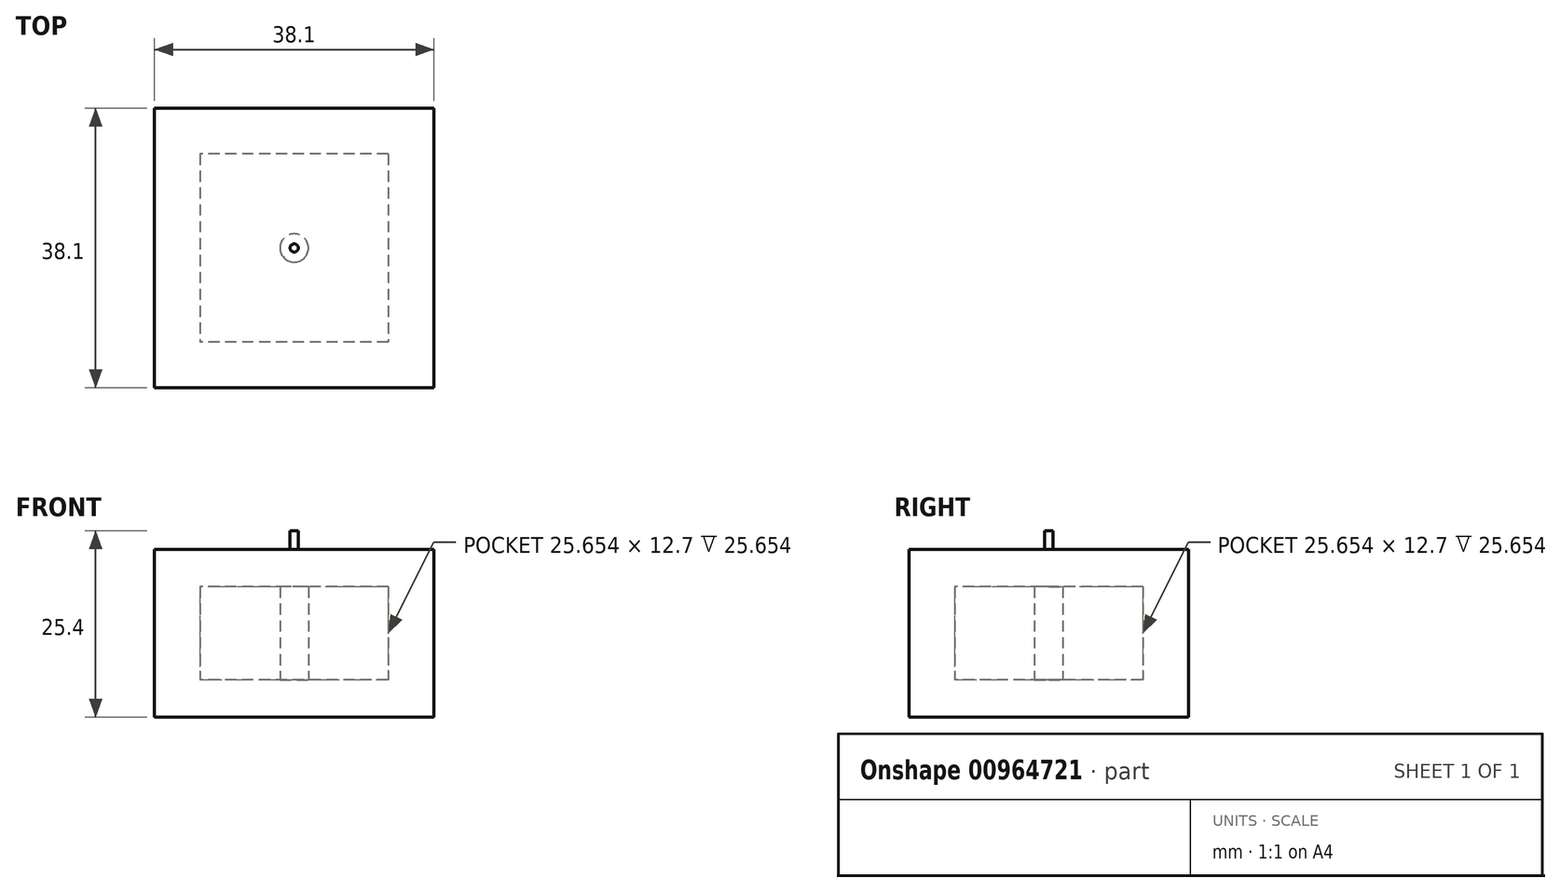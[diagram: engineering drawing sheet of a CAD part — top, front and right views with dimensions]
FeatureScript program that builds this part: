
annotation { "Feature Type Name" : "Feature", "Feature Type Description" : "" }
export const myFeature = defineFeature(function(context is Context, id is Id, definition is map)
    precondition{}
    {
        {
            var Q0;
            Q0=qCreatedBy(makeId("Top.planeOp"),FACE);
            var sketch = newSketch(context, id + "F0", { "sketchPlane" : qUnion([Q0])});
            skLineSegment(sketch, "E0.bottom", {"start": v(19.05, 19.05) * mm, "end": v(-19.05, 19.05) * mm});
            skLineSegment(sketch, "E0.top", {"start": v(19.05, -19.05) * mm, "end": v(-19.05, -19.05) * mm});
            skLineSegment(sketch, "E0.left", {"start": v(19.05, 19.05) * mm, "end": v(19.05, -19.05) * mm});
            skLineSegment(sketch, "E0.right", {"start": v(-19.05, 19.05) * mm, "end": v(-19.05, -19.05) * mm});
            skPoint(sketch, "E0.middle", {"position": v(0, 0) * mm});
            skSolve(sketch);
        }
        {
            var Q0;
            Q0=makeQuery(id+"F0.imprint","IMPRINT",FACE,{"disambiguationData":[TD([[makeQuery(id+"F0.imprint","IMPRINT",EDGE,{"derivedFrom":sQuery(id+"F0.wireOp",EDGE,"E0.bottom")}),1.0]])]});
            extrude(context, id + "F1", {"entities" : qUnion([Q0]), "depth" : 12.7 * mm, "offsetDistance" : 25.4 * mm});
        }
        {
            var Q0;
            Q0=qCreatedBy(makeId("Top.planeOp"),FACE);
            var sketch = newSketch(context, id + "F2", { "sketchPlane" : qUnion([Q0])});
            skLineSegment(sketch, "E1.bottom", {"start": v(12.83, 12.83) * mm, "end": v(-12.83, 12.83) * mm});
            skLineSegment(sketch, "E1.top", {"start": v(12.83, -12.83) * mm, "end": v(-12.83, -12.83) * mm});
            skLineSegment(sketch, "E1.left", {"start": v(12.83, 12.83) * mm, "end": v(12.83, -12.83) * mm});
            skLineSegment(sketch, "E1.right", {"start": v(-12.83, 12.83) * mm, "end": v(-12.83, -12.83) * mm});
            skPoint(sketch, "E1.middle", {"position": v(0, 0) * mm});
            skSolve(sketch);
        }
        {
            var Q0;
            Q0 = qSketchRegion(id + "F2", true);
            extrude(context, id + "F3", {"entities" : qUnion([Q0]), "operationType" : NewBodyOperationType.REMOVE, "depth" : 12.7 * mm, "offsetDistance" : 25.4 * mm});
        }
        {
            var Q0;
            Q0=makeQuery(id+"F1.opExtrude","CAP_FACE",FACE,{"disambiguationData":[OSD([sQuery(id+"F0.wireOp",EDGE,"E0.bottom"),sQuery(id+"F0.wireOp",EDGE,"E0.top"),sQuery(id+"F0.wireOp",EDGE,"E0.left"),sQuery(id+"F0.wireOp",EDGE,"E0.right")])],"isStart":false});
            var sketch = newSketch(context, id + "F4", { "sketchPlane" : qUnion([Q0])});
            skLineSegment(sketch, "E2.bottom", {"start": v(-19.05, -19.05) * mm, "end": v(19.05, -19.05) * mm});
            skLineSegment(sketch, "E2.top", {"start": v(-19.05, 19.05) * mm, "end": v(19.05, 19.05) * mm});
            skLineSegment(sketch, "E2.left", {"start": v(-19.05, -19.05) * mm, "end": v(-19.05, 19.05) * mm});
            skLineSegment(sketch, "E2.right", {"start": v(19.05, -19.05) * mm, "end": v(19.05, 19.05) * mm});
            skSolve(sketch);
        }
        {
            var Q0;
            Q0 = qSketchRegion(id + "F4", true);
            extrude(context, id + "F5", {"entities" : qUnion([Q0]), "operationType" : NewBodyOperationType.ADD, "depth" : 5.08 * mm, "offsetDistance" : 25.4 * mm});
        }
        {
            var Q0;
            Q0=makeQuery(id+"F1.opExtrude","CAP_FACE",FACE,{"disambiguationData":[OSD([sQuery(id+"F0.wireOp",EDGE,"E0.bottom"),sQuery(id+"F0.wireOp",EDGE,"E0.top"),sQuery(id+"F0.wireOp",EDGE,"E0.left"),sQuery(id+"F0.wireOp",EDGE,"E0.right")])],"isStart":true});
            var sketch = newSketch(context, id + "F6", { "sketchPlane" : qUnion([Q0])});
            skLineSegment(sketch, "E3.bottom", {"start": v(-19.05, 19.05) * mm, "end": v(19.05, 19.05) * mm});
            skLineSegment(sketch, "E3.top", {"start": v(-19.05, -19.05) * mm, "end": v(19.05, -19.05) * mm});
            skLineSegment(sketch, "E3.left", {"start": v(-19.05, 19.05) * mm, "end": v(-19.05, -19.05) * mm});
            skLineSegment(sketch, "E3.right", {"start": v(19.05, 19.05) * mm, "end": v(19.05, -19.05) * mm});
            skSolve(sketch);
        }
        {
            var Q0;
            Q0 = qSketchRegion(id + "F6", true);
            extrude(context, id + "F7", {"entities" : qUnion([Q0]), "operationType" : NewBodyOperationType.ADD, "depth" : 5.08 * mm, "offsetDistance" : 25.4 * mm});
        }
        {
            var Q0;
            Q0=makeQuery(id+"F7.opExtrude","CAP_FACE",FACE,{"disambiguationData":[OSD([sQuery(id+"F6.wireOp",EDGE,"E3.bottom"),sQuery(id+"F6.wireOp",EDGE,"E3.top"),sQuery(id+"F6.wireOp",EDGE,"E3.left"),sQuery(id+"F6.wireOp",EDGE,"E3.right")])],"isStart":false});
            var sketch = newSketch(context, id + "F8", { "sketchPlane" : qUnion([Q0])});
            skCircle(sketch, "E4", {"center": v(0, 0) * mm, "radius": 1.94 * mm});
            skSolve(sketch);
        }
        {
            var Q0;
            Q0 = qSketchRegion(id + "F8", true);
            extrude(context, id + "F9", {"entities" : qUnion([Q0]), "operationType" : NewBodyOperationType.ADD, "oppositeDirection" : true, "depth" : 22.6 * mm, "offsetDistance" : 25.4 * mm});
        }
        {
            var Q0;
            Q0=makeQuery(id+"F7.opExtrude","CAP_FACE",FACE,{"disambiguationData":[OSD([sQuery(id+"F6.wireOp",EDGE,"E3.bottom"),sQuery(id+"F6.wireOp",EDGE,"E3.top"),sQuery(id+"F6.wireOp",EDGE,"E3.left"),sQuery(id+"F6.wireOp",EDGE,"E3.right")])],"isStart":false});
            var sketch = newSketch(context, id + "F10", { "sketchPlane" : qUnion([Q0])});
            skCircle(sketch, "E5", {"center": v(0, 0) * mm, "radius": 0.54 * mm});
            skSolve(sketch);
        }
        {
            var Q0;
            Q0 = qSketchRegion(id + "F10", true);
            extrude(context, id + "F11", {"entities" : qUnion([Q0]), "operationType" : NewBodyOperationType.REMOVE, "oppositeDirection" : true, "depth" : 25.4 * mm, "offsetDistance" : 25.4 * mm});
        }
        {
            var Q0;
            Q0=makeQuery(id+"F7.opExtrude","CAP_FACE",FACE,{"disambiguationData":[OSD([sQuery(id+"F6.wireOp",EDGE,"E3.bottom"),sQuery(id+"F6.wireOp",EDGE,"E3.top"),sQuery(id+"F6.wireOp",EDGE,"E3.left"),sQuery(id+"F6.wireOp",EDGE,"E3.right")])],"isStart":false});
            var sketch = newSketch(context, id + "F12", { "sketchPlane" : qUnion([Q0])});
            skCircle(sketch, "E6", {"center": v(0, 0) * mm, "radius": 0.56 * mm});
            skSolve(sketch);
        }
        {
            var Q0;
            Q0 = qSketchRegion(id + "F12", true);
            extrude(context, id + "F13", {"entities" : qUnion([Q0]), "operationType" : NewBodyOperationType.ADD, "oppositeDirection" : true, "depth" : 25.4 * mm, "offsetDistance" : 25.4 * mm});
        }
    });
